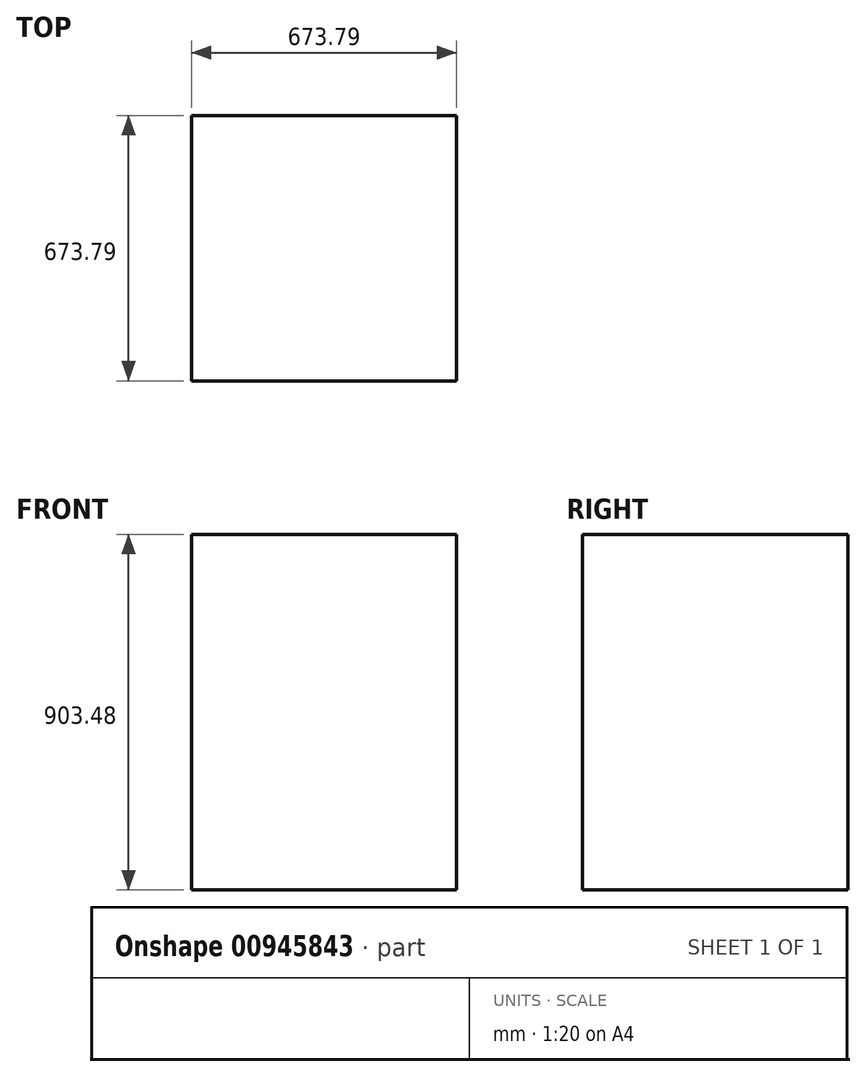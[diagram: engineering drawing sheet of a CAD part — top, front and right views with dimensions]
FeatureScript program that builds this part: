
annotation { "Feature Type Name" : "Feature", "Feature Type Description" : "" }
export const myFeature = defineFeature(function(context is Context, id is Id, definition is map)
    precondition{}
    {
        {
            var Q0;
            Q0=qCreatedBy(makeId("Top.planeOp"),FACE);
            var sketch = newSketch(context, id + "F0", { "sketchPlane" : qUnion([Q0])});
            skLineSegment(sketch, "E0.bottom", {"start": v(-673.79, 673.79) * mm, "end": v(0, 673.79) * mm});
            skLineSegment(sketch, "E0.top", {"start": v(-673.79, 0) * mm, "end": v(0, 0) * mm});
            skLineSegment(sketch, "E0.left", {"start": v(-673.79, 673.79) * mm, "end": v(-673.79, 0) * mm});
            skLineSegment(sketch, "E0.right", {"start": v(0, 673.79) * mm, "end": v(0, 0) * mm});
            skSolve(sketch);
        }
        {
            var Q0;
            Q0=makeQuery(id+"F0.imprint","IMPRINT",FACE,{"disambiguationData":[TD([[makeQuery(id+"F0.imprint","IMPRINT",EDGE,{"derivedFrom":sQuery(id+"F0.wireOp",EDGE,"E0.bottom")}),-1.0]])]});
            extrude(context, id + "F1", {"entities" : qUnion([Q0]), "depth" : 903.48 * mm, "offsetDistance" : 25.4 * mm});
        }
    });
